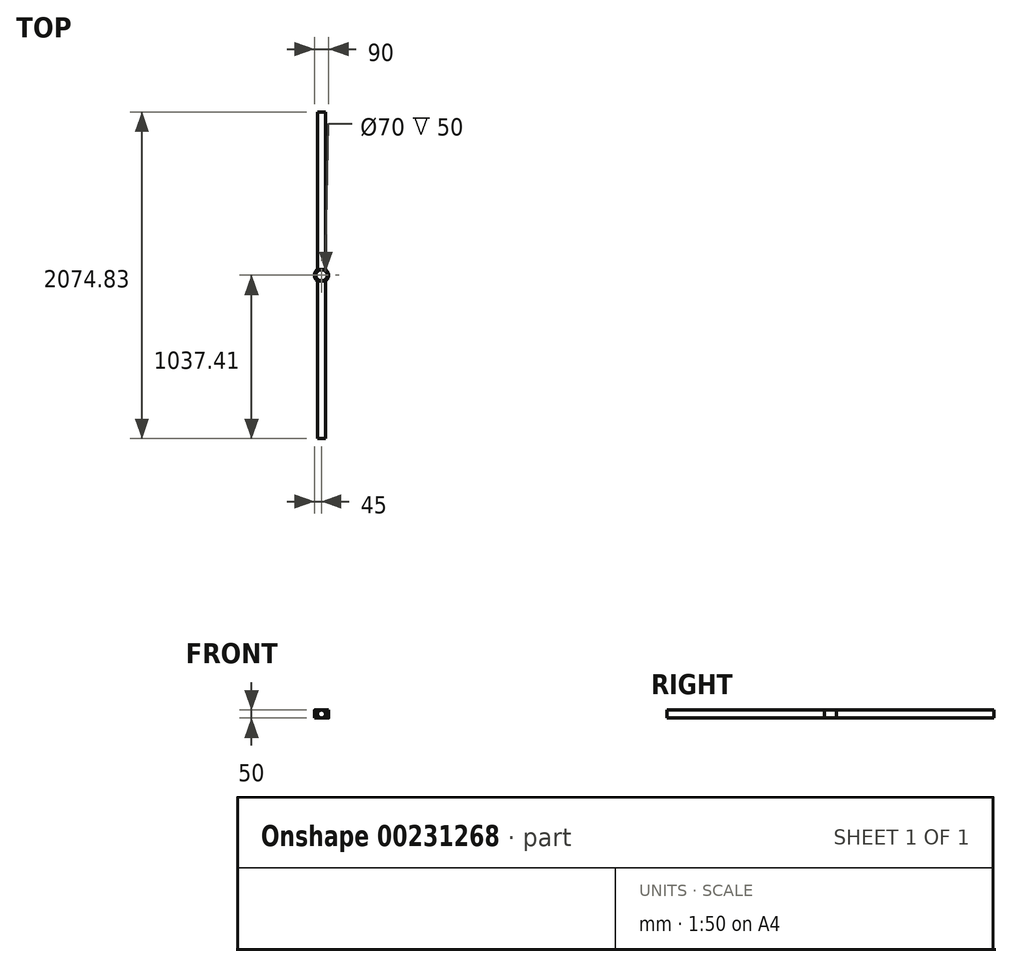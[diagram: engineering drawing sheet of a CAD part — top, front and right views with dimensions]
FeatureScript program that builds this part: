
annotation { "Feature Type Name" : "Feature", "Feature Type Description" : "" }
export const myFeature = defineFeature(function(context is Context, id is Id, definition is map)
    precondition{}
    {
        {
            var Q0;
            Q0=qCreatedBy(makeId("Front.planeOp"),FACE);
            var sketch = newSketch(context, id + "F0", { "sketchPlane" : qUnion([Q0])});
            skCircle(sketch, "E0", {"center": v(0, 0) * mm, "radius": 25 * mm});
            skSolve(sketch);
        }
        {
            var Q0;
            Q0=makeQuery(id+"F0.imprint","IMPRINT",FACE,{"disambiguationData":[TD([[makeQuery(id+"F0.imprint","IMPRINT",EDGE,{"derivedFrom":sQuery(id+"F0.wireOp",EDGE,"E0")}),1.0]])]});
            extrude(context, id + "F1", {"entities" : qUnion([Q0]), "oppositeDirection" : true, "depth" : 1000 * mm});
        }
        {
            var Q0;
            Q0=qCreatedBy(makeId("Top.planeOp"),FACE);
            var sketch = newSketch(context, id + "F2", { "sketchPlane" : qUnion([Q0])});
            skArc(sketch, "E1", {"start": v(-25, 0) * mm, "mid": v(-45, -37.42) * mm, "end": v(-25, -74.83) * mm});
            skCircle(sketch, "E2", {"center": v(0, -37.42) * mm, "radius": 35 * mm});
            skLineSegment(sketch, "E3.0", {"start": v(25, 0) * mm, "end": v(-25, 0) * mm});
            skLineSegment(sketch, "E4", {"start": v(0, -37.42) * mm, "end": v(10.58, -37.42) * mm, "construction": true});
            skArc(sketch, "E5.trimOffspring", {"start": v(25, -74.83) * mm, "mid": v(45, -37.42) * mm, "end": v(25, 0) * mm});
            skLineSegment(sketch, "E6", {"start": v(-25, -74.83) * mm, "end": v(25, -74.83) * mm});
            skSolve(sketch);
        }
        {
            var Q0;
            Q0=makeQuery(id+"F2.imprint","IMPRINT",FACE,{"disambiguationData":[TD([[makeQuery(id+"F2.imprint","IMPRINT",EDGE,{"derivedFrom":sQuery(id+"F2.wireOp",EDGE,"E1")}),1.0]])]});
            extrude(context, id + "F3", {"entities" : qUnion([Q0]), "operationType" : NewBodyOperationType.ADD, "endBound" : BoundingType.SYMMETRIC, "depth" : 50 * mm});
        }
        {
            var Q0;
            Q0=makeQuery(id+"F3.opExtrude","SWEPT_FACE",FACE,{"disambiguationData":[OSD([sQuery(id+"F2.wireOp",EDGE,"E6")])]});
            var sketch = newSketch(context, id + "F4", { "sketchPlane" : qUnion([Q0])});
            skCircle(sketch, "E7.0", {"center": v(0, 0) * mm, "radius": 25 * mm});
            skSolve(sketch);
        }
        {
            var Q0;
            {var subQ0=sQuery(id+"F4.wireOp",EDGE,"E7.0");var subQ1=sQuery(id+"F2.wireOp",EDGE,"E6");var subQ2=makeQuery(id+"F4.imprint","INTERSECT",VERTEX,{"derivedFrom":[makeQuery(id+"F3.opExtrude","CAP_EDGE",EDGE,{"disambiguationData":[OSD([subQ1])],"isStart":false}),subQ0]});Q0=makeQuery(id+"F4.imprint","IMPRINT",FACE,{"disambiguationData":[TD([[makeQuery(id+"F4.imprint","IMPRINT",EDGE,{"disambiguationData":[TD([[subQ2,1.0]])],"derivedFrom":subQ0}),1.0]])]});}
            extrude(context, id + "F5", {"entities" : qUnion([Q0]), "operationType" : NewBodyOperationType.ADD, "depth" : 1000 * mm});
        }
    });
